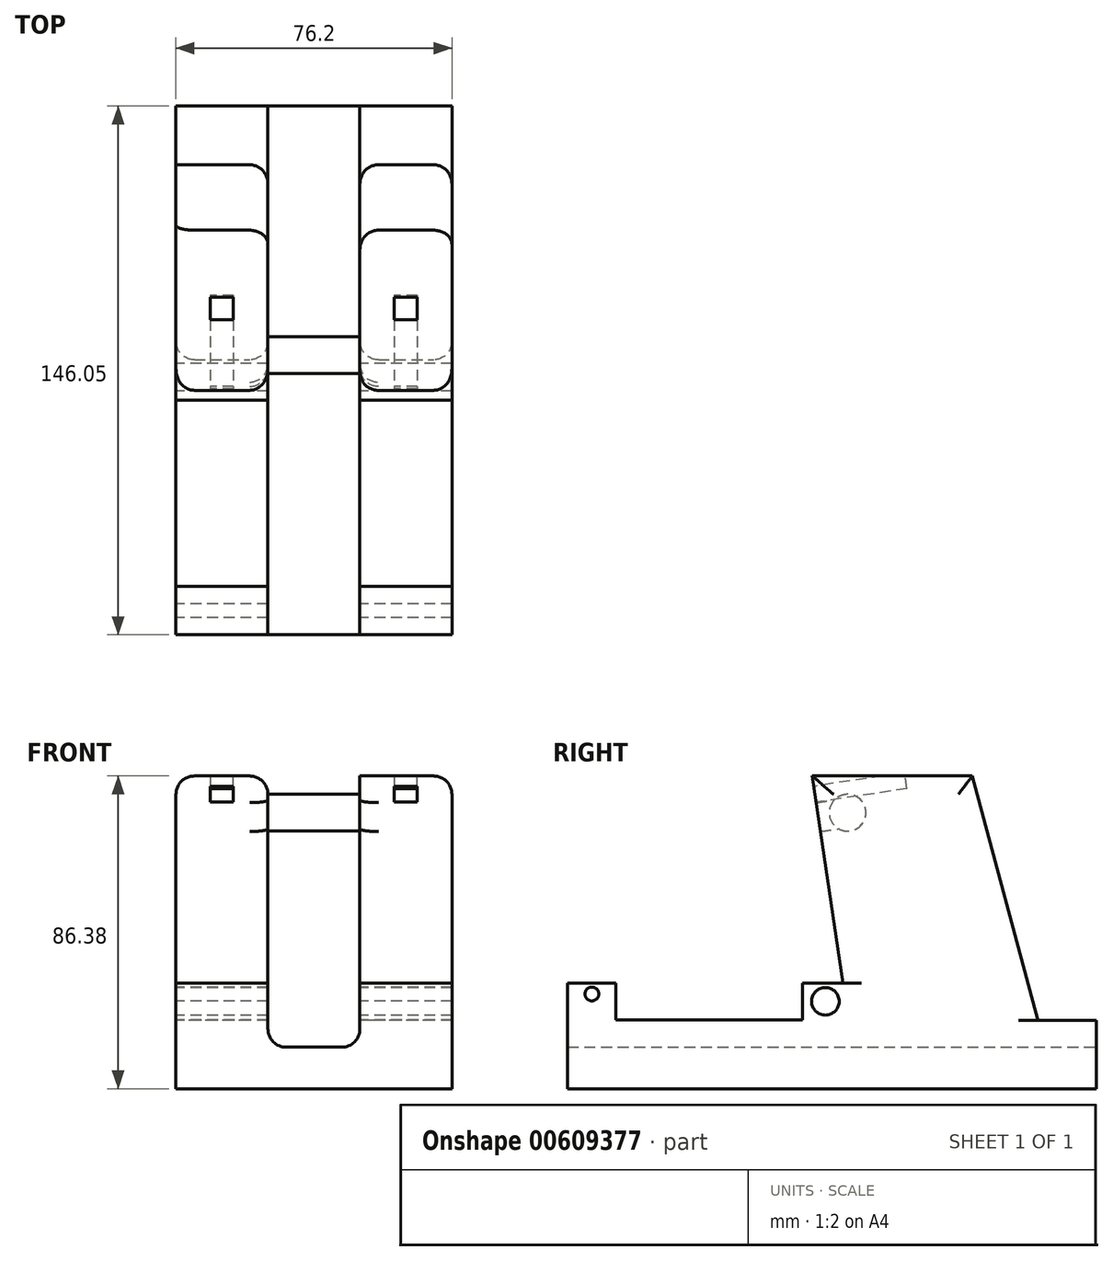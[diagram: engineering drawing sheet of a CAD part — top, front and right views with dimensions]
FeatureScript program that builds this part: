
annotation { "Feature Type Name" : "Feature", "Feature Type Description" : "" }
export const myFeature = defineFeature(function(context is Context, id is Id, definition is map)
    precondition{}
    {
        {
            var Q0;
            Q0=qCreatedBy(makeId("Right.planeOp"),FACE);
            var sketch = newSketch(context, id + "F0", { "sketchPlane" : qUnion([Q0])});
            skLineSegment(sketch, "E0", {"start": v(0, 0) * mm, "end": v(-146.05, 0) * mm});
            skLineSegment(sketch, "E1", {"start": v(-146.05, 0) * mm, "end": v(-146.05, 19.05) * mm});
            skLineSegment(sketch, "E2", {"start": v(-146.05, 19.05) * mm, "end": v(-68.55, 19.05) * mm});
            skLineSegment(sketch, "E3", {"start": v(-68.55, 19.05) * mm, "end": v(-78.52, 86.38) * mm});
            skLineSegment(sketch, "E4", {"start": v(-78.52, 86.38) * mm, "end": v(0, 86.38) * mm});
            skLineSegment(sketch, "E5", {"start": v(0, 86.38) * mm, "end": v(0, 0) * mm});
            skSolve(sketch);
        }
        {
            var Q0;
            Q0 = qSketchRegion(id + "F0", true);
            extrude(context, id + "F1", {"entities" : qUnion([Q0]), "depth" : 38.1 * mm, "offsetDistance" : 25.4 * mm, "hasSecondDirection" : true, "secondDirectionOppositeDirection" : true, "secondDirectionDepth" : 38.1 * mm});
        }
        {
            var Q0;
            Q0=makeQuery(id+"F1.opExtrude","CAP_FACE",FACE,{"disambiguationData":[OSD([sQuery(id+"F0.wireOp",EDGE,"E0"),sQuery(id+"F0.wireOp",EDGE,"E1"),sQuery(id+"F0.wireOp",EDGE,"E2"),sQuery(id+"F0.wireOp",EDGE,"E3"),sQuery(id+"F0.wireOp",EDGE,"E4"),sQuery(id+"F0.wireOp",EDGE,"E5")])],"isStart":true});
            var sketch = newSketch(context, id + "F2", { "sketchPlane" : qUnion([Q0])});
            skLineSegment(sketch, "E6.bottom", {"start": v(146.05, 19.05) * mm, "end": v(132.72, 19.05) * mm});
            skLineSegment(sketch, "E6.top", {"start": v(146.05, 29.21) * mm, "end": v(132.72, 29.21) * mm});
            skLineSegment(sketch, "E6.left", {"start": v(146.05, 19.05) * mm, "end": v(146.05, 29.21) * mm});
            skLineSegment(sketch, "E6.right", {"start": v(132.72, 19.05) * mm, "end": v(132.72, 29.21) * mm});
            skSolve(sketch);
        }
        {
            var Q0;
            Q0 = qSketchRegion(id + "F2", true);
            extrude(context, id + "F3", {"entities" : qUnion([Q0]), "operationType" : NewBodyOperationType.ADD, "oppositeDirection" : true, "depth" : 76.2 * mm, "offsetDistance" : 25.4 * mm});
        }
        {
            var Q0;
            Q0=makeQuery(id+"F1.opExtrude","SWEPT_FACE",FACE,{"disambiguationData":[OSD([sQuery(id+"F0.wireOp",EDGE,"E5")])]});
            var sketch = newSketch(context, id + "F4", { "sketchPlane" : qUnion([Q0])});
            skLineSegment(sketch, "E7.bottom", {"start": v(-12.7, 86.38) * mm, "end": v(12.7, 86.38) * mm});
            skLineSegment(sketch, "E7.top", {"start": v(-12.7, 11.45) * mm, "end": v(12.7, 11.45) * mm});
            skLineSegment(sketch, "E7.left", {"start": v(-12.7, 86.38) * mm, "end": v(-12.7, 11.45) * mm});
            skLineSegment(sketch, "E7.right", {"start": v(12.7, 86.38) * mm, "end": v(12.7, 11.45) * mm});
            skSolve(sketch);
        }
        {
            var Q0;
            Q0 = qSketchRegion(id + "F4", true);
            extrude(context, id + "F5", {"entities" : qUnion([Q0]), "operationType" : NewBodyOperationType.REMOVE, "oppositeDirection" : true, "depth" : 182.37 * mm, "offsetDistance" : 25.4 * mm});
        }
        {
            var Q0;
            Q0=makeQuery(id+"F3.boolean.opBoolean","MERGE",FACE,{"derivedFrom":[makeQuery(id+"F1.opExtrude","CAP_FACE",FACE,{"disambiguationData":[OSD([sQuery(id+"F0.wireOp",EDGE,"E0"),sQuery(id+"F0.wireOp",EDGE,"E1"),sQuery(id+"F0.wireOp",EDGE,"E2"),sQuery(id+"F0.wireOp",EDGE,"E3"),sQuery(id+"F0.wireOp",EDGE,"E4"),sQuery(id+"F0.wireOp",EDGE,"E5")])],"isStart":true}),makeQuery(id+"F3.opExtrude","CAP_FACE",FACE,{"disambiguationData":[OSD([sQuery(id+"F2.wireOp",EDGE,"E6.bottom"),sQuery(id+"F2.wireOp",EDGE,"E6.top"),sQuery(id+"F2.wireOp",EDGE,"E6.left"),sQuery(id+"F2.wireOp",EDGE,"E6.right")])],"isStart":true})]});
            var sketch = newSketch(context, id + "F6", { "sketchPlane" : qUnion([Q0])});
            skCircle(sketch, "E8", {"center": v(139.38, 26.16) * mm, "radius": 1.9 * mm});
            skSolve(sketch);
        }
        {
            var Q0;
            Q0 = qSketchRegion(id + "F6", true);
            extrude(context, id + "F7", {"entities" : qUnion([Q0]), "operationType" : NewBodyOperationType.REMOVE, "oppositeDirection" : true, "depth" : 78.74 * mm, "offsetDistance" : 25.4 * mm});
        }
        {
            var Q0;
            Q0=makeQuery(id+"F3.boolean.opBoolean","MERGE",FACE,{"derivedFrom":[makeQuery(id+"F1.opExtrude","CAP_FACE",FACE,{"disambiguationData":[OSD([sQuery(id+"F0.wireOp",EDGE,"E0"),sQuery(id+"F0.wireOp",EDGE,"E1"),sQuery(id+"F0.wireOp",EDGE,"E2"),sQuery(id+"F0.wireOp",EDGE,"E3"),sQuery(id+"F0.wireOp",EDGE,"E4"),sQuery(id+"F0.wireOp",EDGE,"E5")])],"isStart":true}),makeQuery(id+"F3.opExtrude","CAP_FACE",FACE,{"disambiguationData":[OSD([sQuery(id+"F2.wireOp",EDGE,"E6.bottom"),sQuery(id+"F2.wireOp",EDGE,"E6.top"),sQuery(id+"F2.wireOp",EDGE,"E6.left"),sQuery(id+"F2.wireOp",EDGE,"E6.right")])],"isStart":true})]});
            var sketch = newSketch(context, id + "F8", { "sketchPlane" : qUnion([Q0])});
            skLineSegment(sketch, "E9.bottom", {"start": v(68.55, 19.05) * mm, "end": v(81.25, 19.05) * mm});
            skLineSegment(sketch, "E9.top", {"start": v(68.55, 29.21) * mm, "end": v(81.25, 29.21) * mm});
            skLineSegment(sketch, "E9.left", {"start": v(68.55, 19.05) * mm, "end": v(68.55, 29.21) * mm});
            skLineSegment(sketch, "E9.right", {"start": v(81.25, 19.05) * mm, "end": v(81.25, 29.21) * mm});
            skSolve(sketch);
        }
        {
            var Q0;
            Q0 = qSketchRegion(id + "F8", true);
            extrude(context, id + "F9", {"entities" : qUnion([Q0]), "operationType" : NewBodyOperationType.ADD, "oppositeDirection" : true, "depth" : 76.2 * mm, "offsetDistance" : 25.4 * mm});
        }
        {
            var Q0;
            Q0=makeQuery(id+"F9.opExtrude","SWEPT_FACE",FACE,{"disambiguationData":[OSD([sQuery(id+"F8.wireOp",EDGE,"E9.right")])]});
            var sketch = newSketch(context, id + "F10", { "sketchPlane" : qUnion([Q0])});
            skLineSegment(sketch, "E10.bottom", {"start": v(-12.7, 29.21) * mm, "end": v(12.7, 29.21) * mm});
            skLineSegment(sketch, "E10.top", {"start": v(-12.7, 19.05) * mm, "end": v(12.7, 19.05) * mm});
            skLineSegment(sketch, "E10.left", {"start": v(-12.7, 29.21) * mm, "end": v(-12.7, 19.05) * mm});
            skLineSegment(sketch, "E10.right", {"start": v(12.7, 29.21) * mm, "end": v(12.7, 19.05) * mm});
            skSolve(sketch);
        }
        {
            var Q0;
            Q0 = qSketchRegion(id + "F10", true);
            extrude(context, id + "F11", {"entities" : qUnion([Q0]), "operationType" : NewBodyOperationType.REMOVE, "oppositeDirection" : true, "depth" : 25.4 * mm, "offsetDistance" : 25.4 * mm});
        }
        {
            var Q0;
            Q0=makeQuery(id+"F9.boolean.opBoolean","MERGE",FACE,{"derivedFrom":[makeQuery(id+"F3.boolean.opBoolean","MERGE",FACE,{"derivedFrom":[makeQuery(id+"F1.opExtrude","CAP_FACE",FACE,{"disambiguationData":[OSD([sQuery(id+"F0.wireOp",EDGE,"E0"),sQuery(id+"F0.wireOp",EDGE,"E1"),sQuery(id+"F0.wireOp",EDGE,"E2"),sQuery(id+"F0.wireOp",EDGE,"E3"),sQuery(id+"F0.wireOp",EDGE,"E4"),sQuery(id+"F0.wireOp",EDGE,"E5")])],"isStart":true}),makeQuery(id+"F3.opExtrude","CAP_FACE",FACE,{"disambiguationData":[OSD([sQuery(id+"F2.wireOp",EDGE,"E6.bottom"),sQuery(id+"F2.wireOp",EDGE,"E6.top"),sQuery(id+"F2.wireOp",EDGE,"E6.left"),sQuery(id+"F2.wireOp",EDGE,"E6.right")])],"isStart":true})]}),makeQuery(id+"F9.opExtrude","CAP_FACE",FACE,{"disambiguationData":[OSD([sQuery(id+"F8.wireOp",EDGE,"E9.bottom"),sQuery(id+"F8.wireOp",EDGE,"E9.top"),sQuery(id+"F8.wireOp",EDGE,"E9.left"),sQuery(id+"F8.wireOp",EDGE,"E9.right")])],"isStart":true})]});
            var sketch = newSketch(context, id + "F12", { "sketchPlane" : qUnion([Q0])});
            skCircle(sketch, "E11", {"center": v(74.9, 24.13) * mm, "radius": 3.81 * mm});
            skSolve(sketch);
        }
        {
            var Q0;
            Q0 = qSketchRegion(id + "F12", true);
            extrude(context, id + "F13", {"entities" : qUnion([Q0]), "operationType" : NewBodyOperationType.REMOVE, "oppositeDirection" : true, "depth" : 76.2 * mm, "offsetDistance" : 25.4 * mm});
        }
        {
            var Q0;
            Q0=makeQuery(id+"F9.boolean.opBoolean","MERGE",FACE,{"derivedFrom":[makeQuery(id+"F3.boolean.opBoolean","MERGE",FACE,{"derivedFrom":[makeQuery(id+"F1.opExtrude","CAP_FACE",FACE,{"disambiguationData":[OSD([sQuery(id+"F0.wireOp",EDGE,"E0"),sQuery(id+"F0.wireOp",EDGE,"E1"),sQuery(id+"F0.wireOp",EDGE,"E2"),sQuery(id+"F0.wireOp",EDGE,"E3"),sQuery(id+"F0.wireOp",EDGE,"E4"),sQuery(id+"F0.wireOp",EDGE,"E5")])],"isStart":true}),makeQuery(id+"F3.opExtrude","CAP_FACE",FACE,{"disambiguationData":[OSD([sQuery(id+"F2.wireOp",EDGE,"E6.bottom"),sQuery(id+"F2.wireOp",EDGE,"E6.top"),sQuery(id+"F2.wireOp",EDGE,"E6.left"),sQuery(id+"F2.wireOp",EDGE,"E6.right")])],"isStart":true})]}),makeQuery(id+"F9.opExtrude","CAP_FACE",FACE,{"disambiguationData":[OSD([sQuery(id+"F8.wireOp",EDGE,"E9.bottom"),sQuery(id+"F8.wireOp",EDGE,"E9.top"),sQuery(id+"F8.wireOp",EDGE,"E9.left"),sQuery(id+"F8.wireOp",EDGE,"E9.right")])],"isStart":true})]});
            var sketch = newSketch(context, id + "F14", { "sketchPlane" : qUnion([Q0])});
            skCircle(sketch, "E12", {"center": v(68.75, 76.22) * mm, "radius": 5.08 * mm});
            skSolve(sketch);
        }
        {
            var Q0;
            Q0 = qSketchRegion(id + "F14", true);
            extrude(context, id + "F15", {"entities" : qUnion([Q0]), "operationType" : NewBodyOperationType.ADD, "oppositeDirection" : true, "depth" : 76.2 * mm, "offsetDistance" : 25.4 * mm});
        }
        {
            var Q0;
            Q0=makeQuery(id+"F9.boolean.opBoolean","MERGE",FACE,{"derivedFrom":[makeQuery(id+"F3.boolean.opBoolean","MERGE",FACE,{"derivedFrom":[makeQuery(id+"F1.opExtrude","CAP_FACE",FACE,{"disambiguationData":[OSD([sQuery(id+"F0.wireOp",EDGE,"E0"),sQuery(id+"F0.wireOp",EDGE,"E1"),sQuery(id+"F0.wireOp",EDGE,"E2"),sQuery(id+"F0.wireOp",EDGE,"E3"),sQuery(id+"F0.wireOp",EDGE,"E4"),sQuery(id+"F0.wireOp",EDGE,"E5")])],"isStart":true}),makeQuery(id+"F3.opExtrude","CAP_FACE",FACE,{"disambiguationData":[OSD([sQuery(id+"F2.wireOp",EDGE,"E6.bottom"),sQuery(id+"F2.wireOp",EDGE,"E6.top"),sQuery(id+"F2.wireOp",EDGE,"E6.left"),sQuery(id+"F2.wireOp",EDGE,"E6.right")])],"isStart":true})]}),makeQuery(id+"F9.opExtrude","CAP_FACE",FACE,{"disambiguationData":[OSD([sQuery(id+"F8.wireOp",EDGE,"E9.bottom"),sQuery(id+"F8.wireOp",EDGE,"E9.top"),sQuery(id+"F8.wireOp",EDGE,"E9.left"),sQuery(id+"F8.wireOp",EDGE,"E9.right")])],"isStart":true})]});
            var sketch = newSketch(context, id + "F16", { "sketchPlane" : qUnion([Q0])});
            skLineSegment(sketch, "E13", {"start": v(0, 86.38) * mm, "end": v(34.3, 86.38) * mm});
            skLineSegment(sketch, "E14", {"start": v(34.3, 86.38) * mm, "end": v(16.21, 18.91) * mm});
            skLineSegment(sketch, "E15", {"start": v(16.21, 18.91) * mm, "end": v(0, 18.91) * mm});
            skSolve(sketch);
        }
        {
            var Q0;
            Q0 = qSketchRegion(id + "F16", true);
            var Q1;
            {var subQ0=sQuery(id+"F16.wireOp",EDGE,"E13");Q1=makeQuery(id+"F16.imprint","IMPRINT",FACE,{"disambiguationData":[TD([[makeQuery(id+"F16.imprint","IMPRINT",EDGE,{"derivedFrom":subQ0}),1.0]])]});}
            extrude(context, id + "F17", {"entities" : qUnion([Q0, Q1]), "operationType" : NewBodyOperationType.REMOVE, "oppositeDirection" : true, "depth" : 93.47 * mm, "offsetDistance" : 25.4 * mm});
        }
        {
            var Q0;
            {var subQ2=sQuery(id+"F0.wireOp",EDGE,"E3");Q0=makeQuery(id+"F5.boolean.opBoolean","SPLIT",FACE,{"disambiguationData":[TD([makeQuery(id+"F5.opExtrude","SWEPT_FACE",FACE,{"disambiguationData":[OSD([sQuery(id+"F4.wireOp",EDGE,"E7.right")])]})])],"derivedFrom":makeQuery(id+"F1.opExtrude","SWEPT_FACE",FACE,{"disambiguationData":[OSD([subQ2])]})});}
            var sketch = newSketch(context, id + "F18", { "sketchPlane" : qUnion([Q0])});
            skLineSegment(sketch, "E16.bottom", {"start": v(-22.22, 89.65) * mm, "end": v(-28.57, 89.65) * mm});
            skLineSegment(sketch, "E16.top", {"start": v(-22.22, 94.1) * mm, "end": v(-28.57, 94.1) * mm});
            skLineSegment(sketch, "E16.left", {"start": v(-22.22, 89.65) * mm, "end": v(-22.22, 94.1) * mm});
            skLineSegment(sketch, "E16.right", {"start": v(-28.57, 89.65) * mm, "end": v(-28.57, 94.1) * mm});
            skPoint(sketch, "E16.middle", {"position": v(-25.4, 91.87) * mm});
            skSolve(sketch);
        }
        {
            var Q0;
            Q0 = qSketchRegion(id + "F18", true);
            extrude(context, id + "F19", {"entities" : qUnion([Q0]), "operationType" : NewBodyOperationType.REMOVE, "oppositeDirection" : true, "depth" : 25.4 * mm, "offsetDistance" : 25.4 * mm});
        }
        {
            var Q0;
            {var subQ2=sQuery(id+"F0.wireOp",EDGE,"E3");Q0=makeQuery(id+"F5.boolean.opBoolean","SPLIT",FACE,{"disambiguationData":[TD([makeQuery(id+"F5.opExtrude","SWEPT_FACE",FACE,{"disambiguationData":[OSD([sQuery(id+"F4.wireOp",EDGE,"E7.left")])]})])],"derivedFrom":makeQuery(id+"F1.opExtrude","SWEPT_FACE",FACE,{"disambiguationData":[OSD([subQ2])]})});}
            var sketch = newSketch(context, id + "F20", { "sketchPlane" : qUnion([Q0])});
            skLineSegment(sketch, "E17.bottom", {"start": v(28.57, 89.65) * mm, "end": v(22.22, 89.65) * mm});
            skLineSegment(sketch, "E17.top", {"start": v(28.57, 94.1) * mm, "end": v(22.22, 94.1) * mm});
            skLineSegment(sketch, "E17.left", {"start": v(28.57, 89.65) * mm, "end": v(28.57, 94.1) * mm});
            skLineSegment(sketch, "E17.right", {"start": v(22.22, 89.65) * mm, "end": v(22.22, 94.1) * mm});
            skPoint(sketch, "E17.middle", {"position": v(25.4, 91.87) * mm});
            skSolve(sketch);
        }
        {
            var Q0;
            Q0 = qSketchRegion(id + "F20", true);
            extrude(context, id + "F21", {"entities" : qUnion([Q0]), "operationType" : NewBodyOperationType.REMOVE, "oppositeDirection" : true, "depth" : 25.4 * mm, "offsetDistance" : 25.4 * mm});
        }
        {
            var Q0;
            Q0=makeQuery(id+"F17.boolean.opBoolean","INTERSECT",EDGE,{"derivedFrom":[makeQuery(id+"F11.boolean.opBoolean","MERGE",FACE,{"derivedFrom":[makeQuery(id+"F5.boolean.opBoolean","COPY",FACE,{"derivedFrom":makeQuery(id+"F5.opExtrude","SWEPT_FACE",FACE,{"disambiguationData":[OSD([sQuery(id+"F4.wireOp",EDGE,"E7.right")])]})}),makeQuery(id+"F11.opExtrude","SWEPT_FACE",FACE,{"disambiguationData":[OSD([sQuery(id+"F10.wireOp",EDGE,"E10.left")])]})]}),makeQuery(id+"F17.opExtrude","SWEPT_FACE",FACE,{"disambiguationData":[OSD([sQuery(id+"F16.wireOp",EDGE,"E14")])]})]});
            var Q1;
            Q1=makeQuery(id+"F17.boolean.opBoolean","COPY",EDGE,{"derivedFrom":makeQuery(id+"F17.opExtrude","CAP_EDGE",EDGE,{"disambiguationData":[OSD([sQuery(id+"F16.wireOp",EDGE,"E14")])],"isStart":true})});
            var Q2;
            Q2=makeQuery(id+"F17.boolean.opBoolean","INTERSECT",EDGE,{"derivedFrom":[makeQuery(id+"F11.boolean.opBoolean","MERGE",FACE,{"derivedFrom":[makeQuery(id+"F5.boolean.opBoolean","COPY",FACE,{"derivedFrom":makeQuery(id+"F5.opExtrude","SWEPT_FACE",FACE,{"disambiguationData":[OSD([sQuery(id+"F4.wireOp",EDGE,"E7.left")])]})}),makeQuery(id+"F11.opExtrude","SWEPT_FACE",FACE,{"disambiguationData":[OSD([sQuery(id+"F10.wireOp",EDGE,"E10.right")])]})]}),makeQuery(id+"F17.opExtrude","SWEPT_FACE",FACE,{"disambiguationData":[OSD([sQuery(id+"F16.wireOp",EDGE,"E14")])]})]});
            var Q3;
            Q3=makeQuery(id+"F17.boolean.opBoolean","INTERSECT",EDGE,{"derivedFrom":[makeQuery(id+"F9.boolean.opBoolean","MERGE",FACE,{"derivedFrom":[makeQuery(id+"F3.boolean.opBoolean","MERGE",FACE,{"derivedFrom":[makeQuery(id+"F1.opExtrude","CAP_FACE",FACE,{"disambiguationData":[OSD([sQuery(id+"F0.wireOp",EDGE,"E0"),sQuery(id+"F0.wireOp",EDGE,"E1"),sQuery(id+"F0.wireOp",EDGE,"E2"),sQuery(id+"F0.wireOp",EDGE,"E3"),sQuery(id+"F0.wireOp",EDGE,"E4"),sQuery(id+"F0.wireOp",EDGE,"E5")])],"isStart":false}),makeQuery(id+"F3.opExtrude","CAP_FACE",FACE,{"disambiguationData":[OSD([sQuery(id+"F2.wireOp",EDGE,"E6.bottom"),sQuery(id+"F2.wireOp",EDGE,"E6.top"),sQuery(id+"F2.wireOp",EDGE,"E6.left"),sQuery(id+"F2.wireOp",EDGE,"E6.right")])],"isStart":false})]}),makeQuery(id+"F9.opExtrude","CAP_FACE",FACE,{"disambiguationData":[OSD([sQuery(id+"F8.wireOp",EDGE,"E9.bottom"),sQuery(id+"F8.wireOp",EDGE,"E9.top"),sQuery(id+"F8.wireOp",EDGE,"E9.left"),sQuery(id+"F8.wireOp",EDGE,"E9.right")])],"isStart":false})]}),makeQuery(id+"F17.opExtrude","SWEPT_FACE",FACE,{"disambiguationData":[OSD([sQuery(id+"F16.wireOp",EDGE,"E14")])]})]});
            var Q4;
            Q4=makeQuery(id+"F1.opExtrude","CAP_EDGE",EDGE,{"disambiguationData":[OSD([sQuery(id+"F0.wireOp",EDGE,"E3")])],"isStart":false});
            var Q5;
            Q5=makeQuery(id+"F5.boolean.opBoolean","INTERSECT",EDGE,{"derivedFrom":[makeQuery(id+"F1.opExtrude","SWEPT_FACE",FACE,{"disambiguationData":[OSD([sQuery(id+"F0.wireOp",EDGE,"E3")])]}),makeQuery(id+"F5.opExtrude","SWEPT_FACE",FACE,{"disambiguationData":[OSD([sQuery(id+"F4.wireOp",EDGE,"E7.left")])]})]});
            var Q6;
            Q6=makeQuery(id+"F5.boolean.opBoolean","INTERSECT",EDGE,{"derivedFrom":[makeQuery(id+"F1.opExtrude","SWEPT_FACE",FACE,{"disambiguationData":[OSD([sQuery(id+"F0.wireOp",EDGE,"E3")])]}),makeQuery(id+"F5.opExtrude","SWEPT_FACE",FACE,{"disambiguationData":[OSD([sQuery(id+"F4.wireOp",EDGE,"E7.right")])]})]});
            var Q7;
            Q7=makeQuery(id+"F1.opExtrude","CAP_EDGE",EDGE,{"disambiguationData":[OSD([sQuery(id+"F0.wireOp",EDGE,"E3")])],"isStart":true});
            var Q8;
            Q8=makeQuery(id+"F1.opExtrude","CAP_EDGE",EDGE,{"disambiguationData":[OSD([sQuery(id+"F0.wireOp",EDGE,"E4")])],"isStart":false});
            var Q9;
            Q9=makeQuery(id+"F5.boolean.opBoolean","COPY",EDGE,{"derivedFrom":makeQuery(id+"F5.opExtrude","SWEPT_EDGE",EDGE,{"disambiguationData":[OSD([sQuery(id+"F0.wireOp",EDGE,"E4"),sQuery(id+"F0.wireOp",EDGE,"E5"),sQuery(id+"F4.wireOp",EDGE,"E7.bottom"),sQuery(id+"F4.wireOp",EDGE,"E7.left")])]})});
            var Q10;
            {var subQ0=sQuery(id+"F16.wireOp",EDGE,"E14");var subQ1=sQuery(id+"F0.wireOp",EDGE,"E4");Q10=makeQuery(id+"F17.boolean.opBoolean","COPY",EDGE,{"disambiguationData":[TD([makeQuery(id+"F5.boolean.opBoolean","COPY",FACE,{"derivedFrom":makeQuery(id+"F5.opExtrude","SWEPT_FACE",FACE,{"disambiguationData":[OSD([sQuery(id+"F4.wireOp",EDGE,"E7.left")])]})})])],"derivedFrom":makeQuery(id+"F17.opExtrude","SWEPT_EDGE",EDGE,{"disambiguationData":[OSD([subQ1,sQuery(id+"F16.wireOp",EDGE,"E13"),subQ0])]})});}
            var Q11;
            Q11=makeQuery(id+"F1.opExtrude","CAP_EDGE",EDGE,{"disambiguationData":[OSD([sQuery(id+"F0.wireOp",EDGE,"E4")])],"isStart":true});
            var Q12;
            Q12=makeQuery(id+"F5.boolean.opBoolean","COPY",EDGE,{"derivedFrom":makeQuery(id+"F5.opExtrude","SWEPT_EDGE",EDGE,{"disambiguationData":[OSD([sQuery(id+"F0.wireOp",EDGE,"E4"),sQuery(id+"F0.wireOp",EDGE,"E5"),sQuery(id+"F4.wireOp",EDGE,"E7.bottom"),sQuery(id+"F4.wireOp",EDGE,"E7.right")])]})});
            var Q13;
            {var subQ0=sQuery(id+"F0.wireOp",EDGE,"E4");var subQ1=sQuery(id+"F16.wireOp",EDGE,"E14");Q13=makeQuery(id+"F17.boolean.opBoolean","COPY",EDGE,{"disambiguationData":[TD([makeQuery(id+"F5.boolean.opBoolean","COPY",FACE,{"derivedFrom":makeQuery(id+"F5.opExtrude","SWEPT_FACE",FACE,{"disambiguationData":[OSD([sQuery(id+"F4.wireOp",EDGE,"E7.right")])]})})])],"derivedFrom":makeQuery(id+"F17.opExtrude","SWEPT_EDGE",EDGE,{"disambiguationData":[OSD([subQ0,sQuery(id+"F16.wireOp",EDGE,"E13"),subQ1])]})});}
            var Q14;
            Q14=makeQuery(id+"F5.boolean.opBoolean","COPY",EDGE,{"derivedFrom":makeQuery(id+"F5.opExtrude","SWEPT_EDGE",EDGE,{"disambiguationData":[OSD([sQuery(id+"F4.wireOp",EDGE,"E7.top"),sQuery(id+"F4.wireOp",EDGE,"E7.left")])]})});
            var Q15;
            Q15=makeQuery(id+"F5.boolean.opBoolean","COPY",EDGE,{"derivedFrom":makeQuery(id+"F5.opExtrude","SWEPT_EDGE",EDGE,{"disambiguationData":[OSD([sQuery(id+"F4.wireOp",EDGE,"E7.top"),sQuery(id+"F4.wireOp",EDGE,"E7.right")])]})});
            fillet(context, id + "F22", {"entities" : qUnion([Q0, Q1, Q2, Q3, Q4, Q5, Q6, Q7, Q8, Q9, Q10, Q11, Q12, Q13, Q14, Q15]), "radius" : 5.08 * mm, "tangentPropagation" : true, "allowEdgeOverflow" : false});
        }
    });
